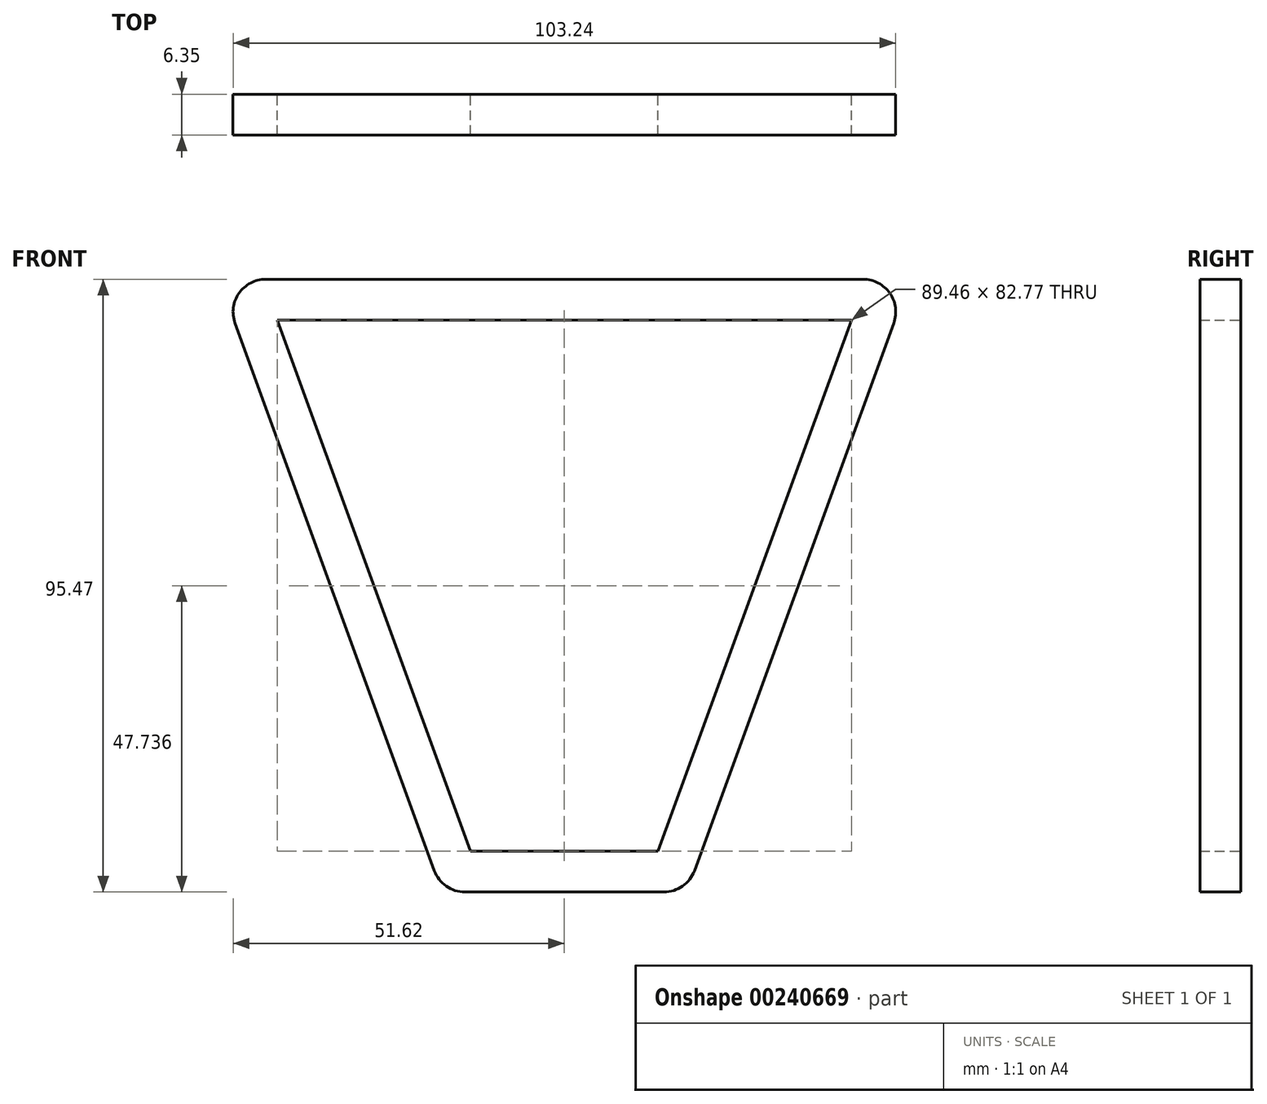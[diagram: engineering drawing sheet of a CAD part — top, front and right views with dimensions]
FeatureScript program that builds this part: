
annotation { "Feature Type Name" : "Feature", "Feature Type Description" : "" }
export const myFeature = defineFeature(function(context is Context, id is Id, definition is map)
    precondition{}
    {
        {
            var Q0;
            Q0=qCreatedBy(makeId("Front.planeOp"),FACE);
            var sketch = newSketch(context, id + "F0", { "sketchPlane" : qUnion([Q0]), "disableImprinting" : false});
            skLineSegment(sketch, "E0", {"start": v(-19.05, 0) * mm, "end": v(19.05, 0) * mm});
            skLineSegment(sketch, "E1", {"start": v(-19.05, 0) * mm, "end": v(-53.8, 95.47) * mm});
            skLineSegment(sketch, "E2", {"start": v(-53.8, 95.47) * mm, "end": v(53.8, 95.47) * mm});
            skLineSegment(sketch, "E3", {"start": v(53.8, 95.47) * mm, "end": v(19.05, 0) * mm});
            skLineSegment(sketch, "E4.0", {"start": v(-14.6, 6.35) * mm, "end": v(-44.73, 89.12) * mm});
            skLineSegment(sketch, "E4.1", {"start": v(-14.6, 6.35) * mm, "end": v(14.6, 6.35) * mm});
            skLineSegment(sketch, "E4.2", {"start": v(44.73, 89.12) * mm, "end": v(14.6, 6.35) * mm});
            skLineSegment(sketch, "E4.3", {"start": v(-44.73, 89.12) * mm, "end": v(44.73, 89.12) * mm});
            skSolve(sketch);
        }
        {
            var Q0;
            Q0=makeQuery(id+"F0.imprint","IMPRINT",FACE,{"disambiguationData":[TD([[makeQuery(id+"F0.imprint","IMPRINT",EDGE,{"derivedFrom":sQuery(id+"F0.wireOp",EDGE,"E0")}),1.0]])]});
            extrude(context, id + "F1", {"entities" : qUnion([Q0]), "depth" : 6.35 * mm});
        }
        {
            var Q0;
            Q0=makeQuery(id+"F1.opExtrude","SWEPT_EDGE",EDGE,{"disambiguationData":[OSD([sQuery(id+"F0.wireOp",EDGE,"E1"),sQuery(id+"F0.wireOp",EDGE,"E2")])]});
            var Q1;
            Q1=makeQuery(id+"F1.opExtrude","SWEPT_EDGE",EDGE,{"disambiguationData":[OSD([sQuery(id+"F0.wireOp",EDGE,"E2"),sQuery(id+"F0.wireOp",EDGE,"E3")])]});
            var Q2;
            Q2=makeQuery(id+"F1.opExtrude","SWEPT_EDGE",EDGE,{"disambiguationData":[OSD([sQuery(id+"F0.wireOp",EDGE,"E0"),sQuery(id+"F0.wireOp",EDGE,"E1")])]});
            var Q3;
            Q3=makeQuery(id+"F1.opExtrude","SWEPT_EDGE",EDGE,{"disambiguationData":[OSD([sQuery(id+"F0.wireOp",EDGE,"E0"),sQuery(id+"F0.wireOp",EDGE,"E3")])]});
            fillet(context, id + "F2", {"entities" : qUnion([Q0, Q1, Q2, Q3]), "radius" : 5.08 * mm, "tangentPropagation" : true, "allowEdgeOverflow" : false});
        }
    });
